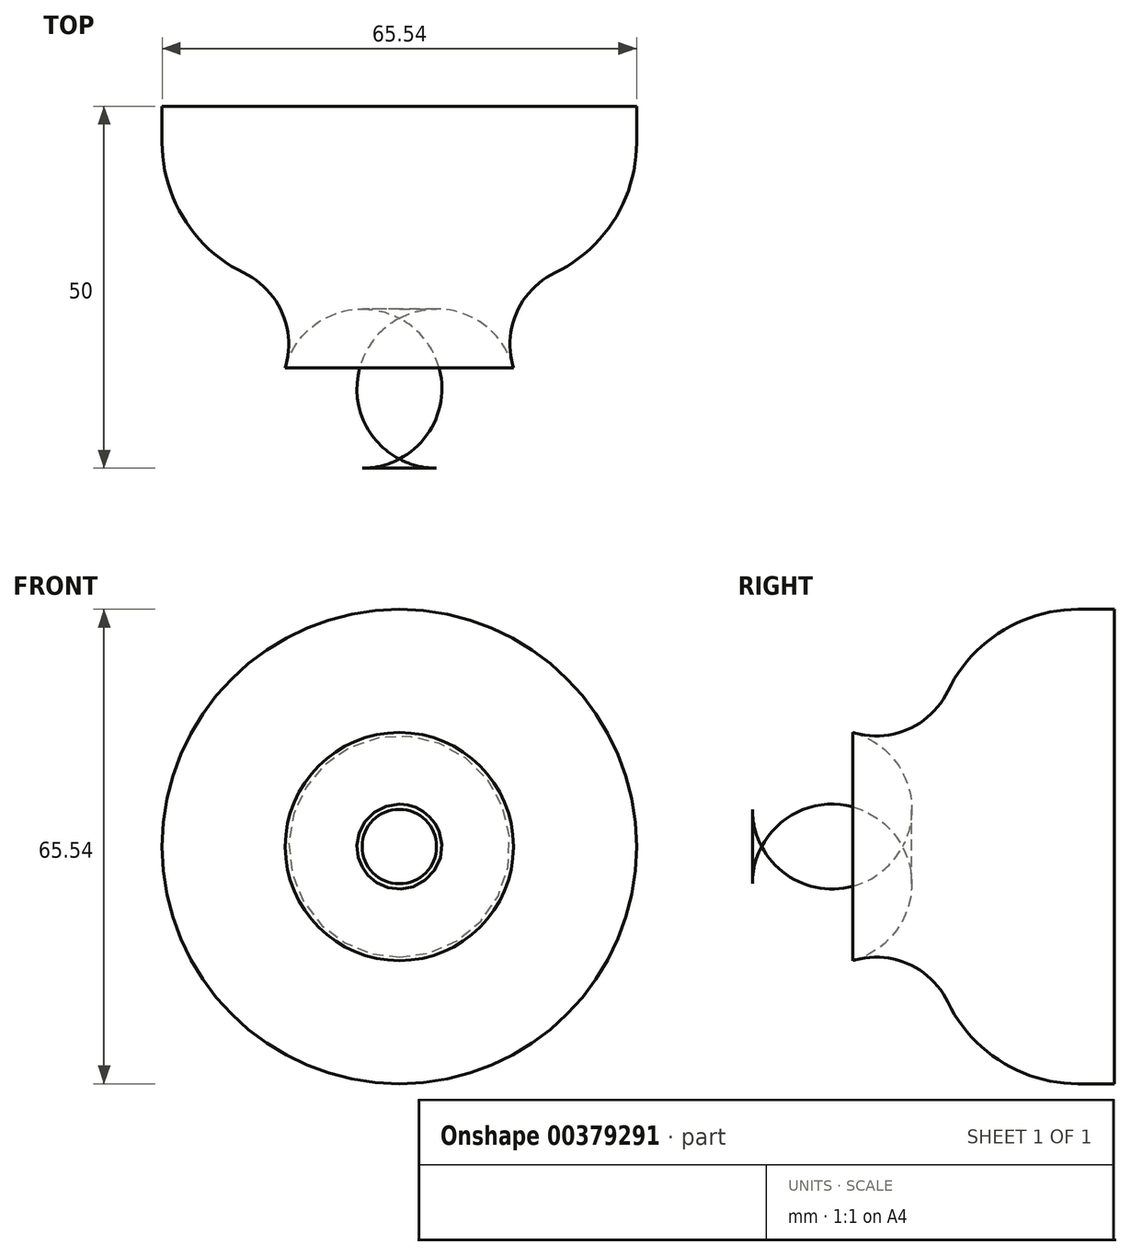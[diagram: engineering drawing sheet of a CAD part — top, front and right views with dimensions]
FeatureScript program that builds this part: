
annotation { "Feature Type Name" : "Feature", "Feature Type Description" : "" }
export const myFeature = defineFeature(function(context is Context, id is Id, definition is map)
    precondition{}
    {
        {
            var Q0;
            Q0=qCreatedBy(makeId("Front.planeOp"),FACE);
            var sketch = newSketch(context, id + "F0", { "sketchPlane" : qUnion([Q0])});
            skCircle(sketch, "E0", {"center": v(0, 0) * mm, "radius": 32.77 * mm});
            skSolve(sketch);
        }
        {
            var Q0;
            Q0 = qSketchRegion(id + "F0", true);
            extrude(context, id + "F1", {"entities" : qUnion([Q0]), "depth" : 25 * mm});
        }
        {
            var Q0;
            Q0=makeQuery(id+"F1.opExtrude","CAP_EDGE",EDGE,{"disambiguationData":[OSD([sQuery(id+"F0.wireOp",EDGE,"E0")])],"isStart":false});
            fillet(context, id + "F2", {"entities" : qUnion([Q0]), "radius" : 20 * mm, "tangentPropagation" : true, "allowEdgeOverflow" : false});
        }
        {
            var Q0;
            Q0=makeQuery(id+"F1.opExtrude","CAP_FACE",FACE,{"disambiguationData":[OSD([sQuery(id+"F0.wireOp",EDGE,"E0")])],"isStart":false});
            extrude(context, id + "F3", {"entities" : qUnion([Q0]), "operationType" : NewBodyOperationType.ADD, "depth" : 25 * mm, "hasDraft" : true, "draftAngle" : 15 * degree});
        }
        {
            var Q0;
            Q0=makeQuery(id+"F3.opExtrude","CAP_EDGE",EDGE,{"disambiguationData":[OSD([sQuery(id+"F0.wireOp",EDGE,"E0")])],"isStart":false});
            var Q1;
            {var subQ0=sQuery(id+"F0.wireOp",EDGE,"E0");Q1=makeQuery(id+"F3.boolean.opBoolean","MERGE",EDGE,{"derivedFrom":[makeQuery(id+"F2.opFillet","BLEND_EDGE",EDGE,{"blendedFrom":[makeQuery(id+"F1.opExtrude","CAP_EDGE",EDGE,{"disambiguationData":[OSD([subQ0])],"isStart":false}),makeQuery(id+"F1.opExtrude","CAP_FACE",FACE,{"disambiguationData":[OSD([subQ0])],"isStart":false})],"blendedInto":[makeQuery(id+"F1.opExtrude","CAP_FACE",FACE,{"disambiguationData":[OSD([subQ0])],"isStart":false})]}),makeQuery(id+"F3.opExtrude","CAP_EDGE",EDGE,{"disambiguationData":[OSD([subQ0])],"isStart":true})]});}
            fillet(context, id + "F4", {"entities" : qUnion([Q0, Q1]), "radius" : 11 * mm, "tangentPropagation" : true, "allowEdgeOverflow" : false});
        }
    });
